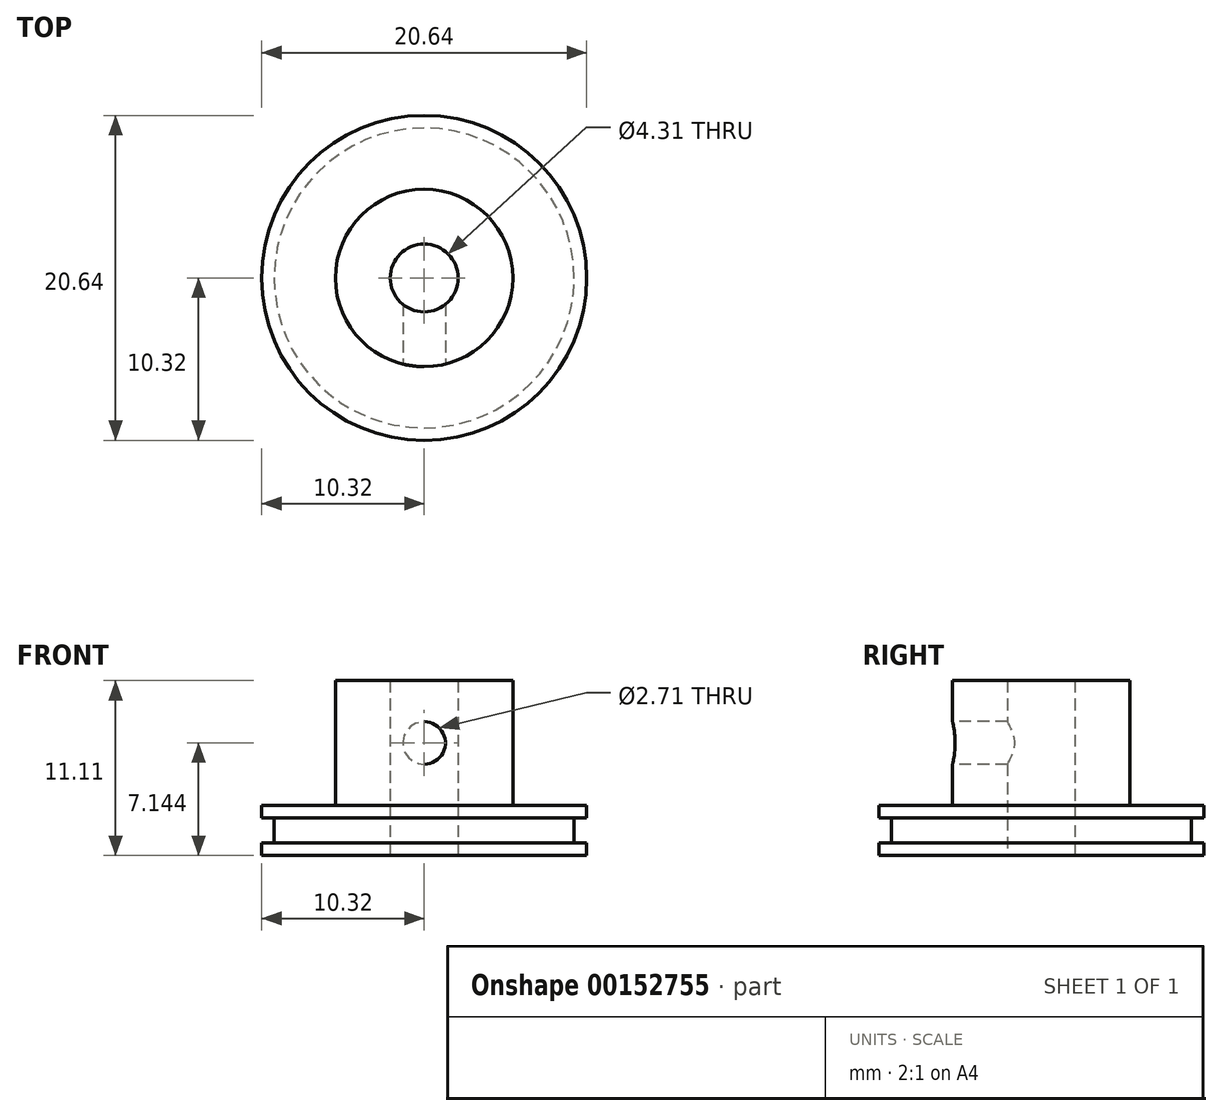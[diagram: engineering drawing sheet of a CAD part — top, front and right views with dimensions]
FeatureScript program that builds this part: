
annotation { "Feature Type Name" : "Feature", "Feature Type Description" : "" }
export const myFeature = defineFeature(function(context is Context, id is Id, definition is map)
    precondition{}
    {
        {
            var Q0;
            Q0=qCreatedBy(makeId("Top.planeOp"),FACE);
            var sketch = newSketch(context, id + "F0", { "sketchPlane" : qUnion([Q0])});
            skCircle(sketch, "E0", {"center": v(0, 0) * mm, "radius": 10.32 * mm});
            skCircle(sketch, "E1", {"center": v(0, 0) * mm, "radius": 2.15 * mm});
            skSolve(sketch);
        }
        {
            var Q0;
            Q0 = qSketchRegion(id + "F0", true);
            extrude(context, id + "F1", {"entities" : qUnion([Q0]), "depth" : 3.17 * mm});
        }
        {
            var Q0;
            Q0=makeQuery(id+"F1.opExtrude","CAP_FACE",FACE,{"disambiguationData":[OSD([sQuery(id+"F0.wireOp",EDGE,"E0"),sQuery(id+"F0.wireOp",EDGE,"E1")])],"isStart":false});
            var sketch = newSketch(context, id + "F2", { "sketchPlane" : qUnion([Q0])});
            skCircle(sketch, "E2", {"center": v(0, 0) * mm, "radius": 2.15 * mm});
            skLineSegment(sketch, "E3.bottom", {"start": v(5.63, -5.63) * mm, "end": v(-5.63, -5.63) * mm});
            skLineSegment(sketch, "E3.top", {"start": v(5.63, 5.63) * mm, "end": v(-5.63, 5.63) * mm});
            skLineSegment(sketch, "E3.left", {"start": v(5.63, -5.63) * mm, "end": v(5.63, 5.63) * mm});
            skLineSegment(sketch, "E3.right", {"start": v(-5.63, -5.63) * mm, "end": v(-5.63, 5.63) * mm});
            skCircle(sketch, "E4", {"center": v(0, 0) * mm, "radius": 5.63 * mm, "construction": true});
            skLineSegment(sketch, "E5.bottom", {"start": v(1.83, 2.15) * mm, "end": v(-1.83, 2.15) * mm, "construction": true});
            skLineSegment(sketch, "E5.top", {"start": v(1.83, 5.33) * mm, "end": v(-1.83, 5.33) * mm, "construction": true});
            skLineSegment(sketch, "E5.left", {"start": v(1.83, 2.15) * mm, "end": v(1.83, 5.33) * mm, "construction": true});
            skLineSegment(sketch, "E5.right", {"start": v(-1.83, 2.15) * mm, "end": v(-1.83, 5.33) * mm, "construction": true});
            skSolve(sketch);
        }
        {
            var Q0;
            Q0 = qSketchRegion(id + "F2", true);
            extrude(context, id + "F3", {"entities" : qUnion([Q0]), "operationType" : NewBodyOperationType.ADD, "depth" : 7.94 * mm});
        }
        {
            var Q0;
            Q0=makeQuery(id+"F3.opExtrude","SWEPT_FACE",FACE,{"disambiguationData":[OSD([sQuery(id+"F2.wireOp",EDGE,"E3.bottom")])]});
            var sketch = newSketch(context, id + "F4", { "sketchPlane" : qUnion([Q0])});
            skLineSegment(sketch, "E6", {"start": v(0, 11.11) * mm, "end": v(0, 3.18) * mm, "construction": true});
            skCircle(sketch, "E7", {"center": v(0, 7.14) * mm, "radius": 1.35 * mm});
            skSolve(sketch);
        }
        {
            var Q0;
            Q0 = qSketchRegion(id + "F4", true);
            var Q1;
            Q1=makeQuery(id+"F3.boolean.opBoolean","MERGE",FACE,{"derivedFrom":[makeQuery(id+"F1.opExtrude","SWEPT_FACE",FACE,{"disambiguationData":[OSD([sQuery(id+"F0.wireOp",EDGE,"E1")])]}),makeQuery(id+"F3.opExtrude","SWEPT_FACE",FACE,{"disambiguationData":[OSD([sQuery(id+"F2.wireOp",EDGE,"E2")])]})]});
            extrude(context, id + "F5", {"entities" : qUnion([Q0]), "operationType" : NewBodyOperationType.REMOVE, "endBound" : BoundingType.UP_TO_SURFACE, "oppositeDirection" : true, "endBoundEntityFace" : qUnion([Q1]), "depth" : 25.4 * mm});
        }
        {
            var Q0;
            Q0=makeQuery(id+"F3.opExtrude","SWEPT_EDGE",EDGE,{"disambiguationData":[OSD([sQuery(id+"F2.wireOp",EDGE,"E3.bottom"),sQuery(id+"F2.wireOp",EDGE,"E3.right")])]});
            var Q1;
            Q1=makeQuery(id+"F3.opExtrude","SWEPT_EDGE",EDGE,{"disambiguationData":[OSD([sQuery(id+"F2.wireOp",EDGE,"E3.bottom"),sQuery(id+"F2.wireOp",EDGE,"E3.left")])]});
            var Q2;
            Q2=makeQuery(id+"F3.opExtrude","SWEPT_EDGE",EDGE,{"disambiguationData":[OSD([sQuery(id+"F2.wireOp",EDGE,"E3.top"),sQuery(id+"F2.wireOp",EDGE,"E3.left")])]});
            var Q3;
            Q3=makeQuery(id+"F3.opExtrude","SWEPT_EDGE",EDGE,{"disambiguationData":[OSD([sQuery(id+"F2.wireOp",EDGE,"E3.top"),sQuery(id+"F2.wireOp",EDGE,"E3.right")])]});
            fillet(context, id + "F6", {"entities" : qUnion([Q0, Q1, Q2, Q3]), "radius" : 5.63 * mm, "tangentPropagation" : true, "allowEdgeOverflow" : false});
        }
        {
            var Q0;
            Q0=qCreatedBy(makeId("Front.planeOp"),FACE);
            var sketch = newSketch(context, id + "F7", { "sketchPlane" : qUnion([Q0])});
            skLineSegment(sketch, "E8.bottom", {"start": v(10.32, 0.8) * mm, "end": v(9.53, 0.8) * mm});
            skLineSegment(sketch, "E8.top", {"start": v(10.32, 2.38) * mm, "end": v(9.53, 2.38) * mm});
            skLineSegment(sketch, "E8.left", {"start": v(10.32, 0.8) * mm, "end": v(10.32, 2.38) * mm});
            skLineSegment(sketch, "E8.right", {"start": v(9.53, 0.8) * mm, "end": v(9.53, 2.38) * mm});
            skLineSegment(sketch, "E9", {"start": v(9.53, 1.59) * mm, "end": v(0, 1.59) * mm, "construction": true});
            skLineSegment(sketch, "E10", {"start": v(0, 1.59) * mm, "end": v(0, 0) * mm, "construction": true});
            skSolve(sketch);
        }
        {
            var Q0;
            Q0 = qSketchRegion(id + "F7", true);
            var Q1;
            Q1=makeQuery(id+"F1.opExtrude","CAP_EDGE",EDGE,{"disambiguationData":[OSD([sQuery(id+"F0.wireOp",EDGE,"E0")])],"isStart":true});
            revolve(context, id + "F8", {"operationType" : NewBodyOperationType.REMOVE, "entities" : qUnion([Q0]), "axis" : qUnion([Q1]), "revolveType" : RevolveType.FULL, "oppositeDirection" : true});
        }
    });
